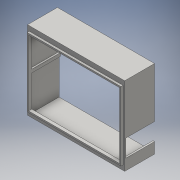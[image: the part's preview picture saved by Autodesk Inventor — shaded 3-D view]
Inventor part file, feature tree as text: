
AUTODESK INVENTOR PART (.ipt)
format: ipt  version: 2016 SP1 (Build 200210100, 210)  size: 183,296 bytes
history: native  units: mm
features: extrude x6, sketch x6, other x3
ambient origin geometry x8: Origin, YZ Plane, XZ Plane, XY Plane, X Axis, Y Axis, Z Axis, Center Point
bodies: Body1 (feature_tree)
feature tree (15):
  other  "Bryła1"
  extrude  "Wyciągnięcie proste1"  Depth=88.0mm
  extrude  "Wyciągnięcie proste2"  Depth=64.5mm
  extrude  "Wyciągnięcie proste3"  Depth=1.5mm
  extrude  "Wyciągnięcie proste4"  Depth=1.5mm
  extrude  "Wyciągnięcie proste5"  Depth=1.5mm
  extrude  "Wyciągnięcie proste6"  Depth=1.5mm
  sketch  "Szkic1"
  sketch  "Szkic2"
  sketch  "Szkic3"
  sketch  "Szkic4"
  sketch  "Szkic5"
  sketch  "Szkic6"
  other  "Rzutuj krawędzie tnące1"
  other  "Rzutuj krawędzie tnące2"
